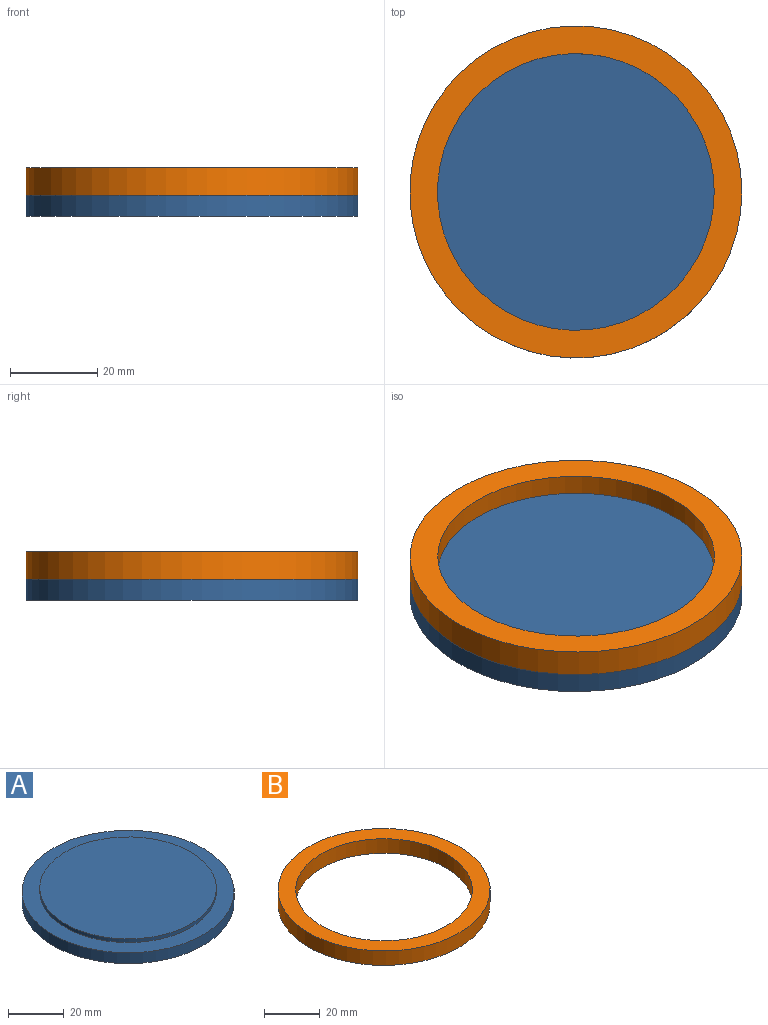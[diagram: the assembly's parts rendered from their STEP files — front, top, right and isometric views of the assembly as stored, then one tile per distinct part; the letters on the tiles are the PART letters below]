
ASSEMBLY  parts=2 mates=1
PART A: 5 faces, bbox 76.2x76.2x6.4 mm
  f0: cylinder r=38.1mm len=76.2mm, axis (0,0,-1), area 1140.1mm2, adj f1,f3
  f1: plane 76.2x76.2mm, normal (0,0,-1), area 4560.4mm2, adj f0
  f2: cylinder r=31.75mm len=63.5mm, axis (0,0,1), area 316.7mm2, adj f3,f4
  f3: plane 76.2x76.2mm, normal (0,0,1), area 1393.4mm2, adj f0,f2
  f4: plane 63.5x63.5mm, normal (0,0,1), area 3166.9mm2, adj f2
PART B: 4 faces, bbox 76.2x76.2x6.4 mm
  f0: cylinder r=31.75mm len=63.5mm, axis (0,0,-1), area 1266.8mm2, adj f2,f3
  f1: cylinder r=38.1mm len=76.2mm, axis (0,0,-1), area 1520.1mm2, adj f2,f3
  f2: plane 76.2x76.2mm, normal (0,0,1), area 1393.4mm2, adj f0,f1
  f3: plane 76.2x76.2mm, normal (0,0,-1), area 1393.4mm2, adj f0,f1
PLACE A t=(0.32,0.06,-3.36)mm
PLACE B t=(0.32,0.06,1.4)mm
MATE planar B.f1 <-> A.f0  axis (0,0,-1) through (0.32,0.06,1.4)mm
